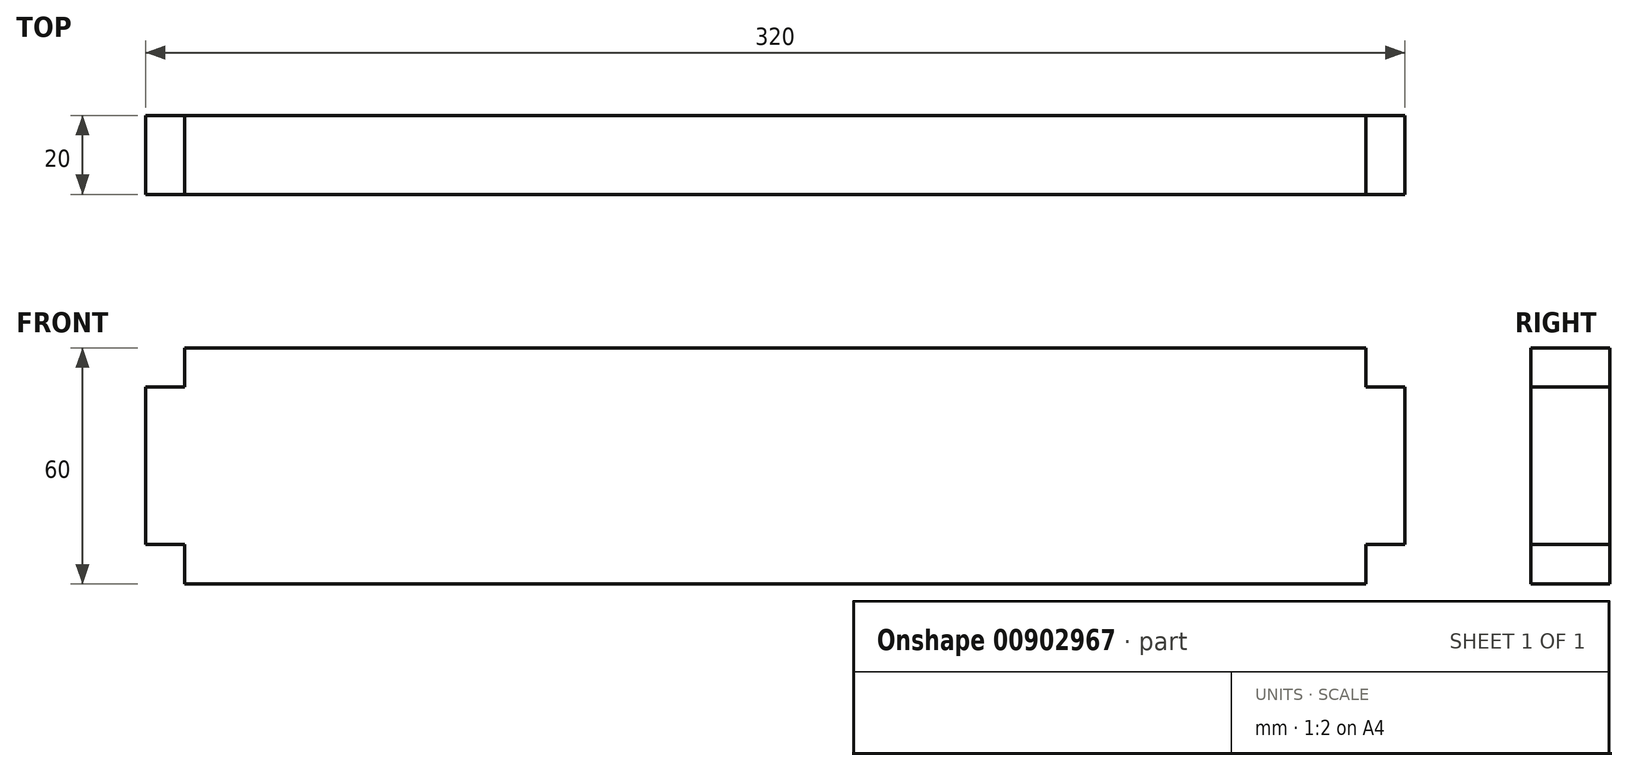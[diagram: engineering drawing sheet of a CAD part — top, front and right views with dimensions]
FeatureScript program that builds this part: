
annotation { "Feature Type Name" : "Feature", "Feature Type Description" : "" }
export const myFeature = defineFeature(function(context is Context, id is Id, definition is map)
    precondition{}
    {
        {
            var Q0;
            Q0=qCreatedBy(makeId("Right.planeOp"),FACE);
            var sketch = newSketch(context, id + "F0", { "sketchPlane" : qUnion([Q0])});
            skLineSegment(sketch, "E0.bottom", {"start": v(0, 0) * mm, "end": v(20, 0) * mm});
            skLineSegment(sketch, "E0.top", {"start": v(0, -60) * mm, "end": v(20, -60) * mm});
            skLineSegment(sketch, "E0.left", {"start": v(0, 0) * mm, "end": v(0, -60) * mm});
            skLineSegment(sketch, "E0.right", {"start": v(20, 0) * mm, "end": v(20, -60) * mm});
            skSolve(sketch);
        }
        {
            var Q0;
            Q0 = qSketchRegion(id + "F0", true);
            extrude(context, id + "F1", {"entities" : qUnion([Q0]), "depth" : 300 * mm, "offsetDistance" : 25 * mm});
        }
        {
            var Q0;
            Q0=makeQuery(id+"F1.opExtrude","CAP_FACE",FACE,{"disambiguationData":[OSD([sQuery(id+"F0.wireOp",EDGE,"E0.bottom"),sQuery(id+"F0.wireOp",EDGE,"E0.top"),sQuery(id+"F0.wireOp",EDGE,"E0.left"),sQuery(id+"F0.wireOp",EDGE,"E0.right")])],"isStart":true});
            var sketch = newSketch(context, id + "F2", { "sketchPlane" : qUnion([Q0])});
            skLineSegment(sketch, "E1.bottom", {"start": v(-20, -10) * mm, "end": v(0, -10) * mm});
            skLineSegment(sketch, "E1.top", {"start": v(-20, -50) * mm, "end": v(0, -50) * mm});
            skLineSegment(sketch, "E1.left", {"start": v(-20, -10) * mm, "end": v(-20, -50) * mm});
            skLineSegment(sketch, "E1.right", {"start": v(0, -10) * mm, "end": v(0, -50) * mm});
            skSolve(sketch);
        }
        {
            var Q0;
            Q0 = qSketchRegion(id + "F2", true);
            extrude(context, id + "F3", {"entities" : qUnion([Q0]), "operationType" : NewBodyOperationType.ADD, "depth" : 10 * mm, "offsetDistance" : 25 * mm});
        }
        {
            var Q0;
            Q0=makeQuery(id+"F1.opExtrude","CAP_FACE",FACE,{"disambiguationData":[OSD([sQuery(id+"F0.wireOp",EDGE,"E0.bottom"),sQuery(id+"F0.wireOp",EDGE,"E0.top"),sQuery(id+"F0.wireOp",EDGE,"E0.left"),sQuery(id+"F0.wireOp",EDGE,"E0.right")])],"isStart":false});
            var sketch = newSketch(context, id + "F4", { "sketchPlane" : qUnion([Q0])});
            skLineSegment(sketch, "E2.bottom", {"start": v(0, -10) * mm, "end": v(20, -10) * mm});
            skLineSegment(sketch, "E2.top", {"start": v(0, -50) * mm, "end": v(20, -50) * mm});
            skLineSegment(sketch, "E2.left", {"start": v(0, -10) * mm, "end": v(0, -50) * mm});
            skLineSegment(sketch, "E2.right", {"start": v(20, -10) * mm, "end": v(20, -50) * mm});
            skSolve(sketch);
        }
        {
            var Q0;
            Q0 = qSketchRegion(id + "F4", true);
            extrude(context, id + "F5", {"entities" : qUnion([Q0]), "operationType" : NewBodyOperationType.ADD, "depth" : 10 * mm, "offsetDistance" : 25 * mm});
        }
    });
